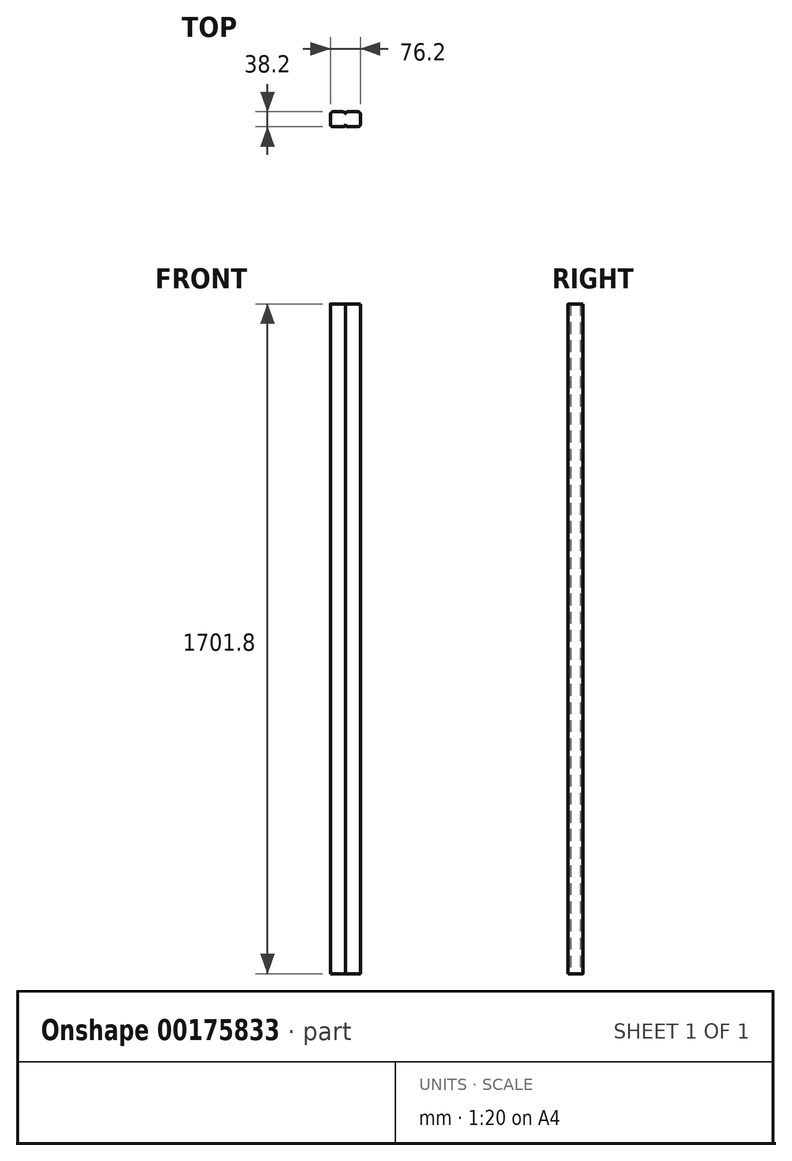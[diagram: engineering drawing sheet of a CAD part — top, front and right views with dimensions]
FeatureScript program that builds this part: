
annotation { "Feature Type Name" : "Feature", "Feature Type Description" : "" }
export const myFeature = defineFeature(function(context is Context, id is Id, definition is map)
    precondition{}
    {
        {
            var Q0;
            Q0=qCreatedBy(makeId("Top.planeOp"),FACE);
            var sketch = newSketch(context, id + "F0", { "sketchPlane" : qUnion([Q0])});
            skLineSegment(sketch, "E0.bottom", {"start": v(-6.35, 18.95) * mm, "end": v(-31.75, 18.95) * mm});
            skLineSegment(sketch, "E0.top", {"start": v(-6.35, -19.15) * mm, "end": v(-31.75, -19.15) * mm});
            skLineSegment(sketch, "E0.left", {"start": v(0, 12.6) * mm, "end": v(0, -12.8) * mm});
            skLineSegment(sketch, "E0.right", {"start": v(-38.1, 12.6) * mm, "end": v(-38.1, -12.8) * mm});
            skPoint(sketch, "E0.middle", {"position": v(-19.05, -0.1) * mm});
            skPoint(sketch, "E1.visualSharp", {"position": v(-38.1, 18.95) * mm});
            skArc(sketch, "E1.filletArc", {"start": v(-31.75, 18.95) * mm, "mid": v(-36.24, 17.09) * mm, "end": v(-38.1, 12.6) * mm});
            skPoint(sketch, "E2.visualSharp", {"position": v(0, 18.95) * mm});
            skArc(sketch, "E2.filletArc", {"start": v(0, 12.6) * mm, "mid": v(-1.86, 17.09) * mm, "end": v(-6.35, 18.95) * mm});
            skPoint(sketch, "E3.visualSharp", {"position": v(0, -19.15) * mm});
            skArc(sketch, "E3.filletArc", {"start": v(-6.35, -19.15) * mm, "mid": v(-1.86, -17.3) * mm, "end": v(0, -12.8) * mm});
            skPoint(sketch, "E4.visualSharp", {"position": v(-38.1, -19.15) * mm});
            skArc(sketch, "E4.filletArc", {"start": v(-38.1, -12.8) * mm, "mid": v(-36.24, -17.3) * mm, "end": v(-31.75, -19.15) * mm});
            skLineSegment(sketch, "E5.bottom", {"start": v(31.75, 19.05) * mm, "end": v(6.35, 19.05) * mm});
            skLineSegment(sketch, "E5.top", {"start": v(31.75, -19.05) * mm, "end": v(6.35, -19.05) * mm});
            skLineSegment(sketch, "E5.left", {"start": v(38.1, 12.7) * mm, "end": v(38.1, -12.7) * mm});
            skLineSegment(sketch, "E5.right", {"start": v(0, 12.7) * mm, "end": v(0, -12.7) * mm});
            skPoint(sketch, "E5.middle", {"position": v(19.05, 0) * mm});
            skPoint(sketch, "E6.visualSharp", {"position": v(0, 19.05) * mm});
            skArc(sketch, "E6.filletArc", {"start": v(6.35, 19.05) * mm, "mid": v(1.86, 17.2) * mm, "end": v(0, 12.7) * mm});
            skPoint(sketch, "E7.visualSharp", {"position": v(38.1, 19.05) * mm});
            skArc(sketch, "E7.filletArc", {"start": v(38.1, 12.7) * mm, "mid": v(36.24, 17.2) * mm, "end": v(31.75, 19.05) * mm});
            skPoint(sketch, "E8.visualSharp", {"position": v(38.1, -19.05) * mm});
            skArc(sketch, "E8.filletArc", {"start": v(31.75, -19.05) * mm, "mid": v(36.24, -17.2) * mm, "end": v(38.1, -12.7) * mm});
            skPoint(sketch, "E9.visualSharp", {"position": v(0, -19.05) * mm});
            skArc(sketch, "E9.filletArc", {"start": v(0, -12.7) * mm, "mid": v(1.86, -17.2) * mm, "end": v(6.35, -19.05) * mm});
            skSolve(sketch);
        }
        {
            var Q0;
            Q0=qSketchRegion(id+"F0",true);
            extrude(context, id + "F1", {"entities" : qUnion([Q0]), "depth" : 1701.8 * mm, "offsetDistance" : 25.4 * mm});
        }
    });
